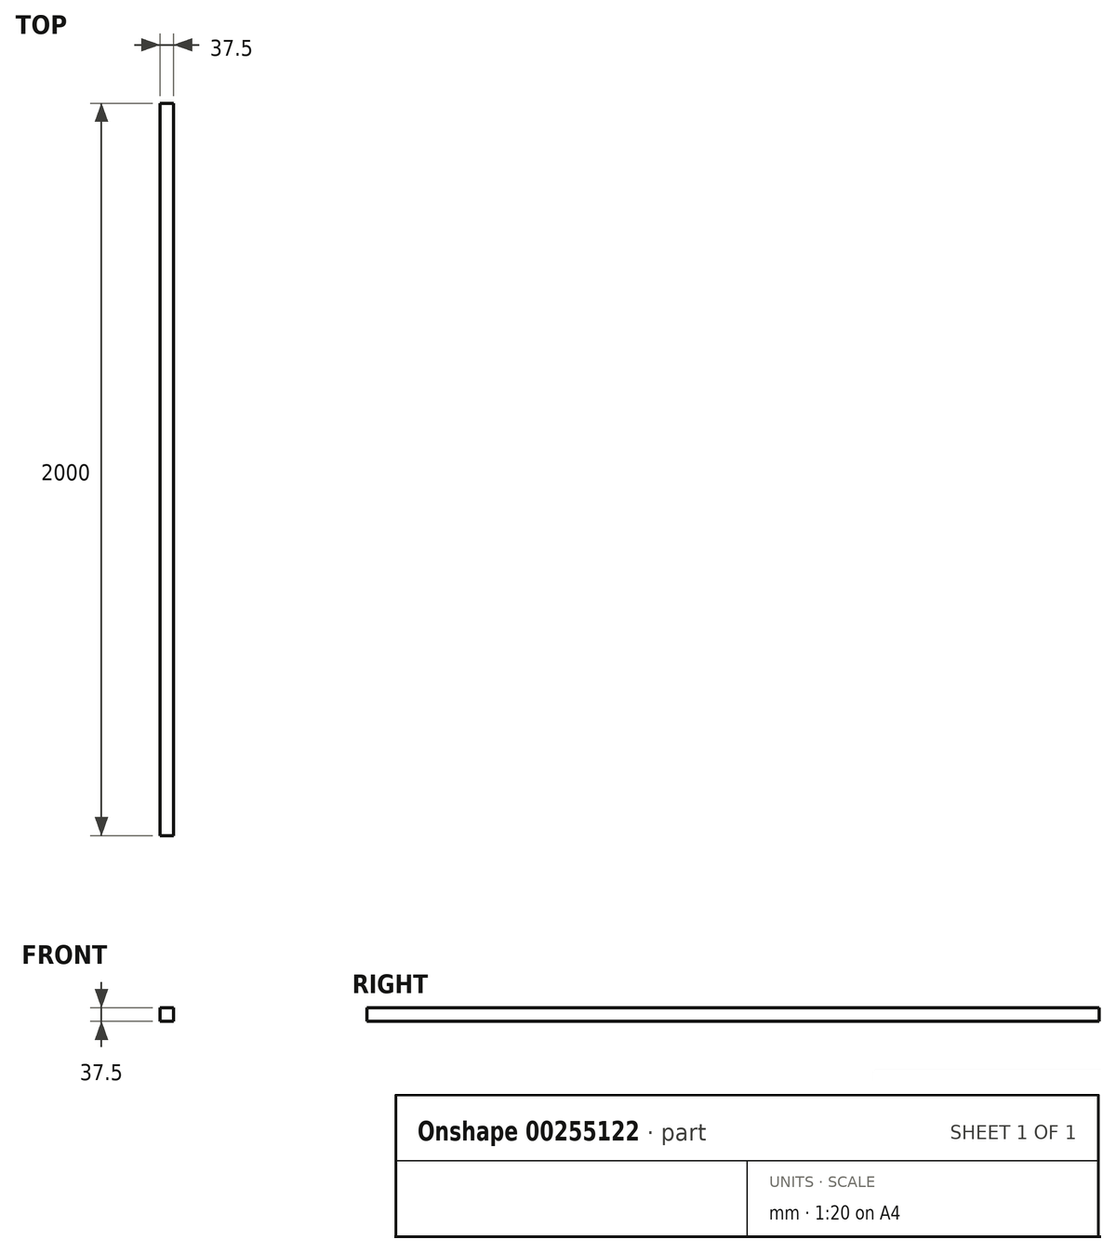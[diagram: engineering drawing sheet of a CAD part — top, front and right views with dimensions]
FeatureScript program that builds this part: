
annotation { "Feature Type Name" : "Feature", "Feature Type Description" : "" }
export const myFeature = defineFeature(function(context is Context, id is Id, definition is map)
    precondition{}
    {
        {
            var Q0;
            Q0=qCreatedBy(makeId("Front.planeOp"),FACE);
            var sketch = newSketch(context, id + "F0", { "sketchPlane" : qUnion([Q0])});
            skLineSegment(sketch, "E0.bottom", {"start": v(18.75, 18.75) * mm, "end": v(-18.75, 18.75) * mm});
            skLineSegment(sketch, "E0.top", {"start": v(18.75, -18.75) * mm, "end": v(-18.75, -18.75) * mm});
            skLineSegment(sketch, "E0.left", {"start": v(18.75, 18.75) * mm, "end": v(18.75, -18.75) * mm});
            skLineSegment(sketch, "E0.right", {"start": v(-18.75, 18.75) * mm, "end": v(-18.75, -18.75) * mm});
            skPoint(sketch, "E0.middle", {"position": v(0, 0) * mm});
            skSolve(sketch);
        }
        {
            var Q0;
            Q0 = qSketchRegion(id + "F0", true);
            extrude(context, id + "F1", {"entities" : qUnion([Q0]), "endBound" : BoundingType.SYMMETRIC, "depth" : 2000 * mm});
        }
    });
